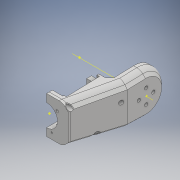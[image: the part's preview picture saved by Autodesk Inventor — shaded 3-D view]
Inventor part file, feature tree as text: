
AUTODESK INVENTOR PART (.ipt)
format: ipt  version: 2018 (Build 220112000, 112)  size: 1,072,640 bytes
history: native  units: mm
features: projected_geometry x48, sketch x45, extrude x37, hole x13, fillet x11, other x10, chamfer x9, reference x3, mirror x1, plane x1
ambient origin geometry x8: Origin, YZ Plane, XZ Plane, XY Plane, X Axis, Y Axis, Z Axis, Center Point
bodies: Solid1 (feature_tree)
feature tree (178):
  extrude  "Extrusion1"  Depth=45.0mm
  extrude  "Extrusion2"  Depth=2.25mm
  hole  "Hole1"  [1 undecoded]
  hole  "Hole2"  [1 undecoded]
  fillet  "Fillet1"  Radius=14.0mm
  extrude  "Extrusion3"  Depth=18.5mm
  extrude  "Extrusion4"  Depth=10.0mm
  extrude  "Extrusion5"  Depth=2.0mm
  extrude  "Extrusion6"  Depth=2.0mm
  hole  "Hole3"  [1 undecoded]
  extrude  "Extrusion7"  Depth=2.0mm
  extrude  "Extrusion8"  Depth=1.0mm TaperAngle=0.0deg
  extrude  "Extrusion9"  Depth=24.5mm
  extrude  "Extrusion10"  Depth=10.0mm
  extrude  "Extrusion11"  Depth=14.5mm
  extrude  "Extrusion13"  Depth=14.5mm
  extrude  "Extrusion14"  Depth=5.0mm
  extrude  "Extrusion15"  Depth=2.25mm
  extrude  "Extrusion16"  Depth=5.0mm
  extrude  "Extrusion17"  Depth=9.0mm
  chamfer  "Chamfer1"  Distance=1.0mm
  fillet  "Fillet7"  Radius=20.7mm
  fillet  "Fillet8"  Radius=32.0mm
  mirror  "Mirror1"
  sketch  "Sketch26"  dims[d55=2.25mm d56=5.0mm]
  extrude  "Extrusion24"  Depth=1.0mm TaperAngle=0.0deg
  extrude  "Extrusion25"  Depth=8.0mm
  extrude  "Extrusion26"  Depth=0.2mm TaperAngle=0.0deg
  extrude  "Extrusion27"  Depth=5.0mm TaperAngle=0.0deg
  other  "Work Axis1"
  plane  "Work Plane2"
  extrude  "Extrusion28"  Depth=0.2mm TaperAngle=0.0deg
  extrude  "Extrusion29"  Depth=2.0mm TaperAngle=45.0deg
  chamfer  "Chamfer2"  Distance=15.0mm
  extrude  "Extrusion31"  Depth=15.0mm TaperAngle=0.0deg
  chamfer  "Chamfer3"  Distance=15.0mm
  chamfer  "Chamfer4"  Distance=100.0mm
  extrude  "Extrusion32"  Depth=2.0mm TaperAngle=45.0deg
  chamfer  "Chamfer5"  [1 undecoded]
  extrude  "Extrusion33"  Depth=1.5mm
  sketch  "Sketch41"  dims[d100=0.2mm d101=0.0mm d102=2.5mm d103=2.0mm d104=45.0deg]
  extrude  "Extrusion34"  Depth=1.5mm
  chamfer  "Chamfer6"  Distance=11.5mm
  fillet  "Fillet9"  Radius=100.0mm
  extrude  "Extrusion35"  Depth=2.0mm TaperAngle=45.0deg
  extrude  "Extrusion36"  Depth=2.0mm TaperAngle=45.0deg
  chamfer  "Chamfer7"  Distance=7.0mm
  fillet  "Fillet10"  Radius=100.0mm
  extrude  "Extrusion37"  Depth=2.0mm TaperAngle=45.0deg
  extrude  "Extrusion38"  Depth=1.5mm TaperAngle=0.0deg
  extrude  "Extrusion39"  Depth=1.5mm TaperAngle=0.0deg
  extrude  "Extrusion40"  Depth=2.0mm TaperAngle=45.0deg
  chamfer  "Chamfer8"  Distance=8.0mm
  chamfer  "Chamfer9"  Angle=15.0deg  [1 undecoded]
  hole  "Hole6"  [1 undecoded]
  fillet  "Fillet11"  Radius=15.470628mm
  fillet  "Fillet12"  Radius=2.5mm
  extrude  "Extrusion41"  Depth=1.5mm TaperAngle=0.0deg
  extrude  "Extrusion42"  Depth=2.0mm TaperAngle=45.0deg
  hole  "Hole7"  [1 undecoded]
  extrude  "Extrusion43"  TaperAngle=15.0deg  [1 undecoded]
  extrude  "Extrusion44"  Depth=1.5mm
  sketch  "Sketch58"  dims[d162=5.0mm d165=100.0mm d166=0.0mm]
  hole  "Hole8"  [1 undecoded]
  hole  "Hole9"  [1 undecoded]
  hole  "Hole10"  [1 undecoded]
  hole  "Hole11"  [1 undecoded]
  hole  "Hole12"  [1 undecoded]
  hole  "Hole13"  [1 undecoded]
  hole  "Hole14"  [1 undecoded]
  hole  "Hole15"  [1 undecoded]
  extrude  "Extrusion45"  Depth=2.0mm
  fillet  "Fillet14"  Radius=0.75mm
  fillet  "Fillet15"  Radius=20.5mm
  fillet  "Fillet16"  Radius=3.05mm
  fillet  "Fillet17"  Radius=14.0mm
  sketch  "Sketch1"  dims[d0=24.5mm d1=45.0mm]
  sketch  "Sketch2"  dims[d2=1.95mm d3=0.0mm d4=2.25mm]
  projected_geometry  "Projected Loop1"
  sketch  "Sketch3"  dims[d5=20.0mm d6=2.25mm]
  projected_geometry  "Projected Loop2"
  sketch  "Sketch4"  dims[d7=5.25mm d8=5.25mm d9=14.0mm]
  projected_geometry  "Projected Loop3"
  sketch  "Sketch5"  dims[d10=5.25mm d11=18.5mm]
  projected_geometry  "Projected Loop4"
  sketch  "Sketch6"  dims[d12=10.0mm d13=0.0mm d14=20.5mm]
  projected_geometry  "Projected Loop5"
  sketch  "Sketch7"  dims[d15=2.0mm d16=2.195mm]
  projected_geometry  "Projected Loop6"
  sketch  "Sketch8"  dims[d17=2.0mm]
  projected_geometry  "Projected Loop7"
  sketch  "Sketch9"  dims[d18=2.4mm d19=6.0mm d20=4.4mm d21=2.0mm d22=90.0deg d23=8.0mm d24=20.594885mm d25=20.5mm]
  projected_geometry  "Projected Loop8"
  projected_geometry  "Projected Loop9"
  sketch  "Sketch10"  dims[d26=26.65mm d27=2.0mm]
  projected_geometry  "Projected Loop10"
  projected_geometry  "Projected Loop11"
  sketch  "Sketch11"  dims[d28=2.0mm]
  projected_geometry  "Projected Loop12"
  sketch  "Sketch12"  dims[d29=2.4mm d30=6.0mm d31=4.4mm d32=2.0mm d33=90.0deg d34=8.0mm d35=20.594885mm d36=0.5mm]
  sketch  "Sketch13"  dims[d37=18.0mm d38=1.0mm d39=0.0mm]
  sketch  "Sketch14"  dims[d41=5.0mm d42=0.0mm d43=24.5mm]
  projected_geometry  "Projected Loop13"
  sketch  "Sketch16"  dims[d44=1.15mm d45=0.0mm d46=10.0mm]
  projected_geometry  "Projected Loop14"
  sketch  "Sketch17"  dims[d47=21.0mm d48=14.5mm]
  projected_geometry  "Projected Loop15"
  sketch  "Sketch18"  dims[d49=20.0mm d50=14.5mm]
  projected_geometry  "Projected Loop16"
  sketch  "Sketch19"  dims[d51=24.5mm d52=5.0mm]
  projected_geometry  "Projected Loop17"
  sketch  "Sketch20"  dims[d53=5.0mm d54=2.25mm]
  projected_geometry  "Projected Loop18"
  projected_geometry  "Projected Loop25"
  sketch  "Sketch31"  dims[d57=5.0mm d58=9.0mm]
  projected_geometry  "Projected Loop30"
  reference  "Reference1"
  sketch  "Sketch32"  dims[d59=14.75mm]
  projected_geometry  "Projected Loop31"
  sketch  "Sketch33"  dims[d60=4.0mm d61=1.0mm d62=0.0mm d63=20.7mm]
  projected_geometry  "Projected Loop32"
  sketch  "Sketch34"  dims[d64=2.4mm d65=6.0mm d66=4.4mm d67=2.0mm d68=90.0deg d69=8.0mm d70=20.594885mm d72=32.0mm]
  projected_geometry  "Projected Loop33"
  other  "Work Point1"
  other  "Work Point2"
  other  "Work Point3"
  sketch  "Sketch35"  dims[d73=3.0mm d74=0.0mm d75=1.0mm d76=0.0mm]
  sketch  "Sketch37"  dims[d77=12.25mm d78=0.0mm d80=8.0mm]
  projected_geometry  "Projected Loop34"
  sketch  "Sketch38"  dims[d81=4.5mm d82=0.0mm d84=0.2mm d85=0.0mm]
  sketch  "Sketch39"  dims[d91=8.0mm d92=0.0mm d93=5.0mm d94=0.0mm]
  sketch  "Sketch40"  dims[d95=5.0mm d96=0.0mm d98=0.2mm d99=0.0mm]
  projected_geometry  "Projected Loop35"
  projected_geometry  "Projected Loop36"
  projected_geometry  "Projected Loop37"
  projected_geometry  "Projected Loop38"
  sketch  "Sketch42"  dims[d105=1.5mm]
  projected_geometry  "Projected Loop39"
  sketch  "Sketch43"  dims[d114=0.5mm]
  reference  "Reference2"
  reference  "Reference3"
  sketch  "Sketch45"  dims[d130=60.0mm]
  projected_geometry  "Projected Loop40"
  sketch  "Sketch46"  dims[d131=36.0mm]
  projected_geometry  "Projected Loop41"
  sketch  "Sketch48"  dims[d146=40.0mm]
  projected_geometry  "Projected Loop43"
  sketch  "Sketch49"  dims[d147=60.0mm]
  projected_geometry  "Projected Loop44"
  projected_geometry  "Projected Loop45"
  sketch  "Sketch50"  dims[d148=0.0mm]
  projected_geometry  "Projected Loop46"
  sketch  "Sketch52"  dims[d149=2.3mm d150=15.0mm d151=0.0mm]
  sketch  "Sketch53"  dims[d152=15.0mm d153=0.0mm d154=15.0mm d155=0.0mm d156=15.0mm d157=0.0mm]
  projected_geometry  "Projected Loop47"
  sketch  "Sketch54"  dims[d158=20.5mm]
  projected_geometry  "Projected Loop48"
  sketch  "Sketch55"  dims[d159=41.5mm]
  sketch  "Sketch56"  dims[d160=15.5mm]
  projected_geometry  "Projected Loop49"
  sketch  "Sketch57"  dims[d161=15.5mm]
  projected_geometry  "Projected Loop50"
  projected_geometry  "Projected Loop51"
  projected_geometry  "Projected Loop52"
  projected_geometry  "Projected Loop53"
  projected_geometry  "Projected Loop54"
  projected_geometry  "Projected Loop55"
  projected_geometry  "Projected Loop56"
  projected_geometry  "Projected Loop57"
  sketch  "Sketch59"  dims[d167=100.0mm d168=0.0mm d169=6.0mm d170=2.0mm d171=45.0deg d172=0.0mm d173=11.5mm d175=11.5mm d176=11.5mm d179=100.0mm d180=0.0mm d181=5.0mm d182=2.0mm d183=45.0deg d184=5.0mm d185=2.0mm d186=45.0deg d187=7.0mm d188=100.0mm d189=0.0mm d190=5.0mm d191=2.0mm d192=45.0deg d193=100.0mm d194=0.0mm d195=100.0mm d196=0.0mm d197=5.0mm d198=2.0mm d199=45.0deg d200=8.0mm d202=15.0deg d204=10.970628mm d205=15.470628mm d206=2.5mm d207=0.0mm d208=2.5mm d209=0.0mm d210=3.0mm d211=2.0mm d212=45.0deg d213=2.0mm d215=15.0deg d216=4.0mm d217=4.0mm d218=5.0mm d219=0.0mm d222=32.0mm d223=4.0mm d224=0.0mm d225=2.5mm d226=0.0mm d227=6.5mm d228=0.0mm d229=3.0mm d230=2.0mm d231=45.0deg d232=3.0mm d233=2.0mm d234=45.0deg d235=1.567mm d236=15.0mm d237=4.0mm d238=2.0mm d239=90.0deg d240=15.0mm d241=20.594885mm d242=2.0mm d243=0.75mm d244=20.5mm d245=3.05mm d246=0.0mm d247=14.0mm d248=3.2mm d249=6.0mm d250=4.0mm d251=2.0mm d252=90.0deg d253=8.8mm d254=20.594885mm d255=20.5mm d256=1.55mm d257=0.0mm d258=8.0mm d259=2.5mm d260=0.0mm d261=8.0mm d262=2.5mm d263=0.0mm d266=4.624622mm d267=4.624622mm d268=2.75mm d269=2.75mm d270=2.35mm d271=2.35mm d272=14.0mm d273=4.0mm d274=5.6mm d275=3.708mm d276=3.023mm d277=2.0mm d278=14.3117mm d279=17.0mm d280=0.0mm d281=4.0mm d282=3.708mm d283=3.023mm d284=2.0mm d285=14.3117mm d286=19.0mm d287=0.0mm d288=4.0mm d289=3.708mm d290=3.023mm d291=2.0mm d292=14.3117mm d293=13.0mm d294=0.0mm d295=2.3mm d296=4.0mm d297=4.4mm d298=2.0mm d299=90.0deg d300=32.25mm d301=0.0mm d302=3.3mm d303=4.0mm d304=6.3mm d305=2.0mm d306=90.0deg d307=32.25mm d308=0.0mm d309=1.567mm d310=4.0mm d311=6.3mm d312=2.0mm d313=90.0deg d314=45.0mm d315=20.594885mm d316=1.567mm d317=4.0mm d318=6.3mm d319=2.0mm d320=90.0deg d321=55.0mm d322=20.594885mm d323=2.459mm d324=6.0mm d325=6.3mm d326=2.0mm d327=90.0deg d328=50.0mm d329=20.594885mm d330=32.25mm d331=0.0mm d333=0.5mm d334=0.4mm d335=1.0mm d336=1.5mm]
  parser-record x1  (decoder bookkeeping rows leaked as tree rows — omitted from the tree; the rows remain in map.json)
  other  "servocheck.iam"
  other  "LX-16A:3"
  other  "DUOPAN-SG-SJ_10"
  projected_geometry  "Project Cut Edges1"
  projected_geometry  "Project Cut Edges3"
  other  "bottomarm:1"
  other  "arm1:1"
note: 16 required parameter values undecoded (feature->parameter linkage not recoverable at this tier; creation-order binding heuristic only, values carry confidence <= 0.55)
note: 1 file-system path scrubbed to <path> (originals preserved in map.json)
